# Revit family: Sanitary_Zurn_ZH8820-XL-LR-Q-PC-ZH8824-XL-LRLK-Q-PC _Angle_Stop
name_source: partatom
category: Plumbing Fixtures
units: mm (PartAtom-declared; Revit-internal decimal feet)

## family parameters
Cut with Voids When Loaded = No
Host = Face
Maintain Annotation Orientation = No
OmniClass Number = 23.45.55.11
OmniClass Title = Sanitary Components
Part Type = Normal
Room Calculation Point = No
Round Connector Dimension = Use Radius
Shared = No

## types (8) — shared parameters
Assembly Code = D2010410
Description = Quarter-Turn Heavy-Duty Stop with Flexible Lavatory Supply
Finish = Chrome-Plated Brass - Zurn - Polished
Flange = Yes
LR Visibility (Supply Kit Copper Risers) = Yes
Manufacturer = Zurn
Manufacturer Brand = Zurn Water, LLC
Modified Date = 03/27/2026
Outlet Connection Size = 0.375 "
Product Documentation Link = https://files.zurn.com
Product Page URL = https://www.zurn.com
Product data URL = https://bimobject.com
URL = https://www.zurn.com
Vent Connection = No
Waste Connection = No
zero-valued in all types: CWFU, Default Elevation, HWFU, WFU

## per-type parameters (varying)
| type | Handle Wheel ( Default Handle) | Inlet Connection Size | Loose Key (-LK) | Model |
| ZH8820-XL-LRQ-PC (3/8 IPS x 3/8  OD) | Yes | 0.375 " | No | ZH8820-XL-LRQ-PC |
| ZH8820-XL-LRLKQ-PC (3/8 IPS x 3/8 OD) | No | 0.375 " | Yes | ZH8820-XL-LRLKQ-PC |
| ZH8822-XL-LRQ-PC (1/2 IPS x 3/8 OD) | Yes | 0.5 " | No | ZH8822-XL-LRQ-PC |
| ZH8822-XL-LRLKQ-PC (1/2  IPS x 3/8 OD) | No | 0.5 " | Yes | ZH8822-XL-LRLKQ-PC |
| ZH8824-XL-LRQ-PC (1/2 NOM x 3/8 OD) | Yes | 0.5 " | No | ZH8824-XL-LRQ-PC |
| ZH8824-XL-LRLKQ-PC (1/2 NOM x 3/8 OD) | No | 0.5 " | Yes | ZH8824-XL-LRLKQ-PC |
| ZH8826-XL-LR-PC (1/2 SWT x 3/8 OD) | Yes | 0.5 " | No | ZH8826-XL-LR-PC |
| ZH8826-XL-LRLK-PC (1/2 SWT x 3/8 OD) | No | 0.5 " | Yes | ZH8826-XL-LRLK-PC |

note: column(s) folded — value = type name in every type: Type Comments

## geometry (parser evidence)
native form markers: Blend x4, Sweep x13
no freeform markers — native parametric forms only
